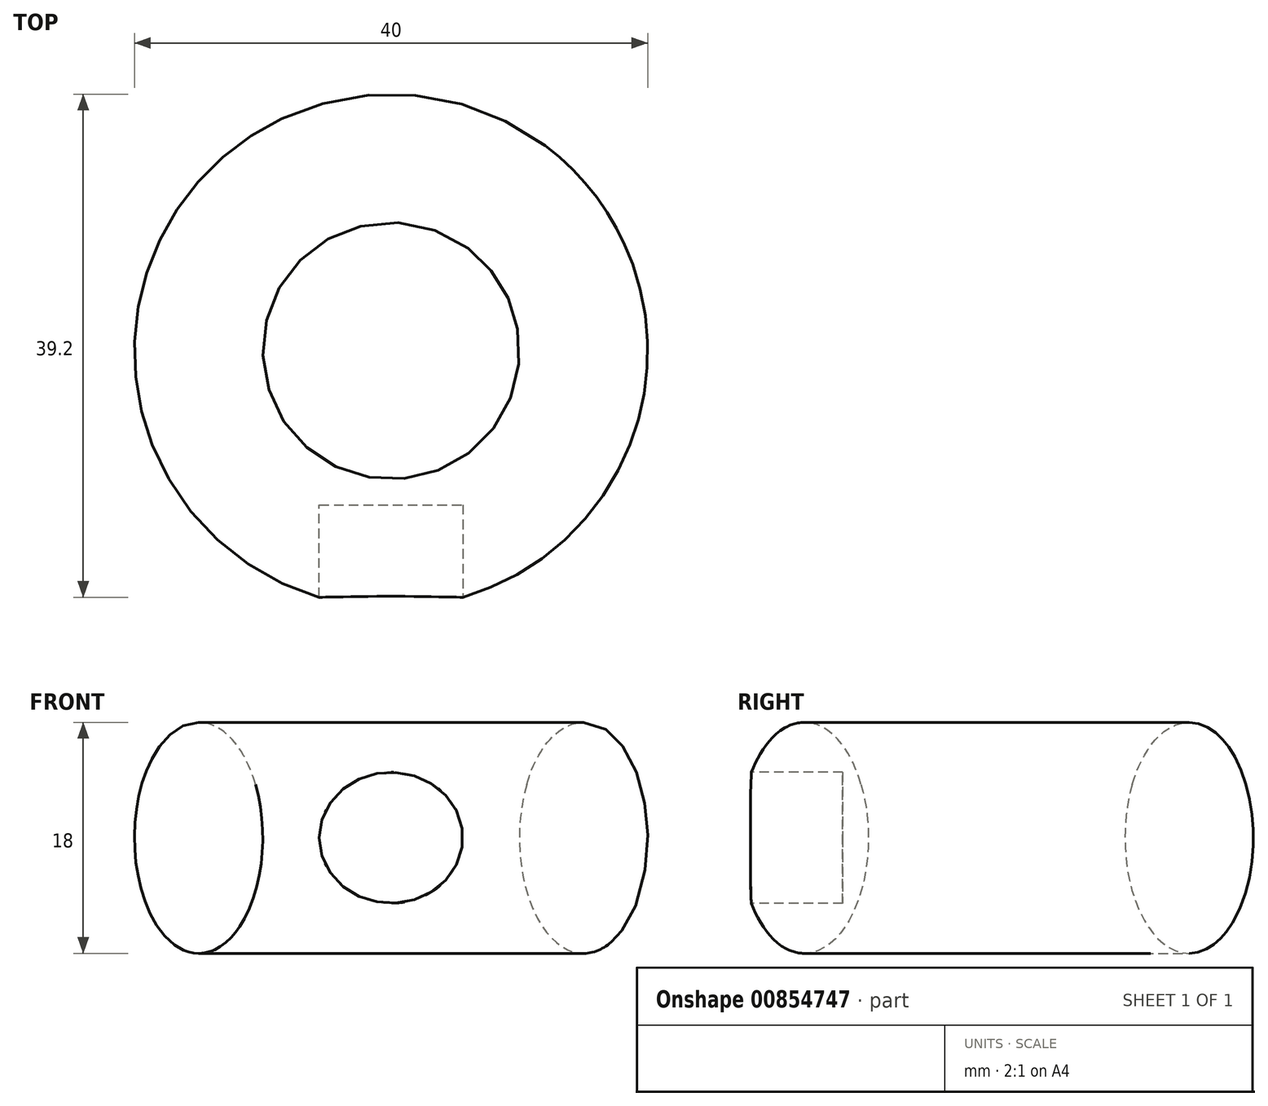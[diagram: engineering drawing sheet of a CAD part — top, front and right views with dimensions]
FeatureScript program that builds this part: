
annotation { "Feature Type Name" : "Feature", "Feature Type Description" : "" }
export const myFeature = defineFeature(function(context is Context, id is Id, definition is map)
    precondition{}
    {
        {
            var Q0;
            Q0=qCreatedBy(makeId("Front.planeOp"),FACE);
            var sketch = newSketch(context, id + "F0", { "sketchPlane" : qUnion([Q0])});
            skLineSegment(sketch, "E0", {"start": v(0, 0) * mm, "end": v(0, 44.53) * mm, "construction": true});
            skEllipse(sketch, "E1", {"center": v(-15, 34.25) * mm, "majorRadius": 9 * mm, "minorRadius": 5 * mm, "majorAxis": v(0, -1)});
            skSolve(sketch);
        }
        {
            var Q0;
            Q0 = qSketchRegion(id + "F0", true);
            var Q1;
            Q1=sQuery(id+"F0.wireOp",EDGE,"E0");
            revolve(context, id + "F1", {"surfaceOperationType" : NewSurfaceOperationType.NEW, "entities" : qUnion([Q0]), "axis" : qUnion([Q1]), "revolveType" : RevolveType.FULL});
        }
        {
            var Q0;
            Q0=qCreatedBy(makeId("Front.planeOp"),FACE);
            cPlane(context, id + "F2", {"entities" : qUnion([Q0]), "cplaneType" : CPlaneType.OFFSET, "offset" : 12 * mm, "width" : 150 * mm, "height" : 150 * mm});
        }
        {
            var Q0;
            Q0=qCreatedBy(id+"F2.planeOp",FACE);
            var sketch = newSketch(context, id + "F3", { "sketchPlane" : qUnion([Q0])});
            skEllipse(sketch, "E2", {"center": v(0, 34.26) * mm, "majorRadius": 5.6 * mm, "minorRadius": 5.1 * mm, "majorAxis": v(-1, 0)});
            skSolve(sketch);
        }
        {
            var Q0;
            Q0 = qSketchRegion(id + "F3", true);
            extrude(context, id + "F4", {"entities" : qUnion([Q0]), "operationType" : NewBodyOperationType.REMOVE, "depth" : 25 * mm, "offsetDistance" : 25 * mm});
        }
    });
